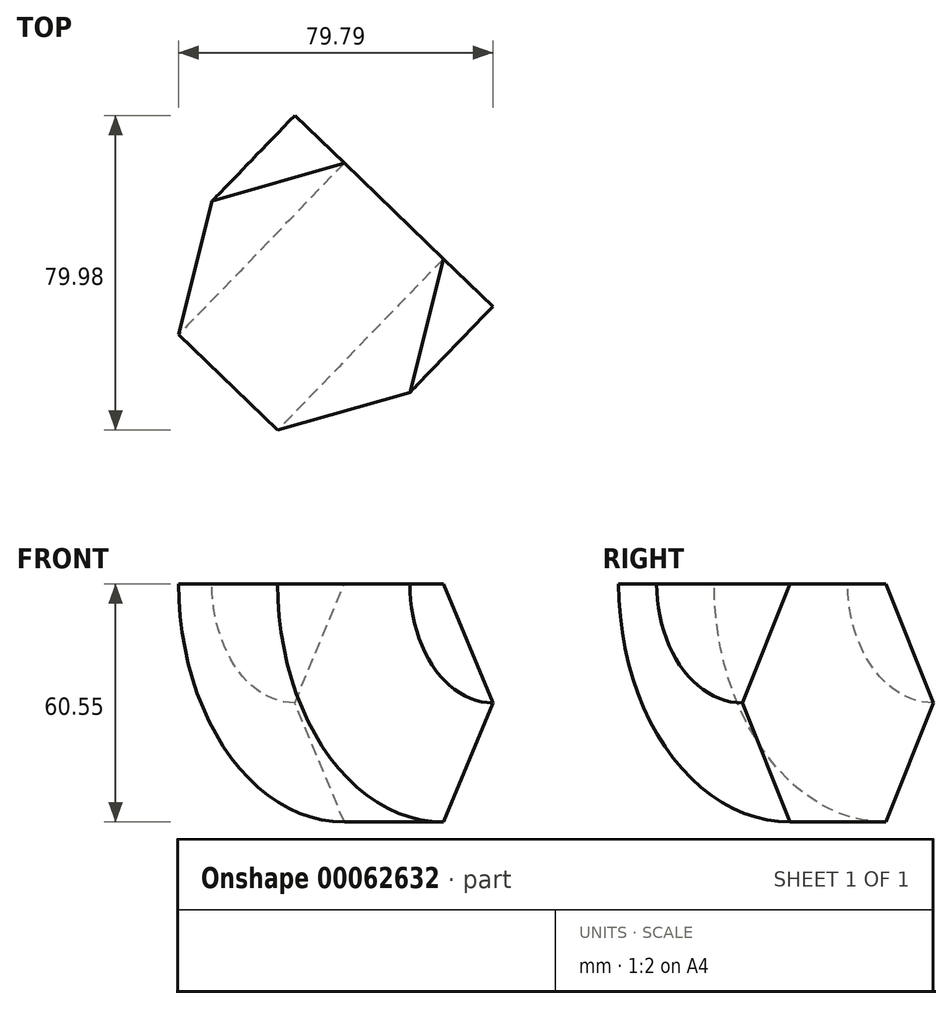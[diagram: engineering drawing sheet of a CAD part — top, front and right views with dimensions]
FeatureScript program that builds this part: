
annotation { "Feature Type Name" : "Feature", "Feature Type Description" : "" }
export const myFeature = defineFeature(function(context is Context, id is Id, definition is map)
    precondition{}
    {
        {
            var Q0;
            Q0=qCreatedBy(makeId("Top.planeOp"),FACE);
            var sketch = newSketch(context, id + "F0", { "sketchPlane" : qUnion([Q0])});
            skCircle(sketch, "E0.cCircle", {"center": v(0, 0) * mm, "radius": 30.28 * mm, "construction": true});
            skLineSegment(sketch, "E0.0", {"start": v(8.46, 33.92) * mm, "end": v(33.6, 9.63) * mm});
            skLineSegment(sketch, "E0.1", {"start": v(33.6, 9.63) * mm, "end": v(25.15, -24.29) * mm});
            skLineSegment(sketch, "E0.2", {"start": v(25.15, -24.29) * mm, "end": v(-8.46, -33.92) * mm});
            skLineSegment(sketch, "E0.3", {"start": v(-8.46, -33.92) * mm, "end": v(-33.6, -9.63) * mm});
            skLineSegment(sketch, "E0.4", {"start": v(-33.6, -9.63) * mm, "end": v(-25.15, 24.29) * mm});
            skLineSegment(sketch, "E0.5", {"start": v(-25.15, 24.29) * mm, "end": v(8.46, 33.92) * mm});
            skPoint(sketch, "E0.0.midPoint", {"position": v(21.03, 21.78) * mm});
            skSolve(sketch);
        }
        {
            var Q0;
            Q0=makeQuery(id+"F0.imprint","IMPRINT",FACE,{"disambiguationData":[TD([[makeQuery(id+"F0.imprint","IMPRINT",EDGE,{"derivedFrom":sQuery(id+"F0.wireOp",EDGE,"E0.0")}),-1.0]])]});
            var Q1;
            Q1=sQuery(id+"F0.wireOp",EDGE,"E0.0");
            revolve(context, id + "F1", {"entities" : qUnion([Q0]), "axis" : qUnion([Q1]), "revolveType" : RevolveType.ONE_DIRECTION, "angle" : 90 * degree});
        }
    });
